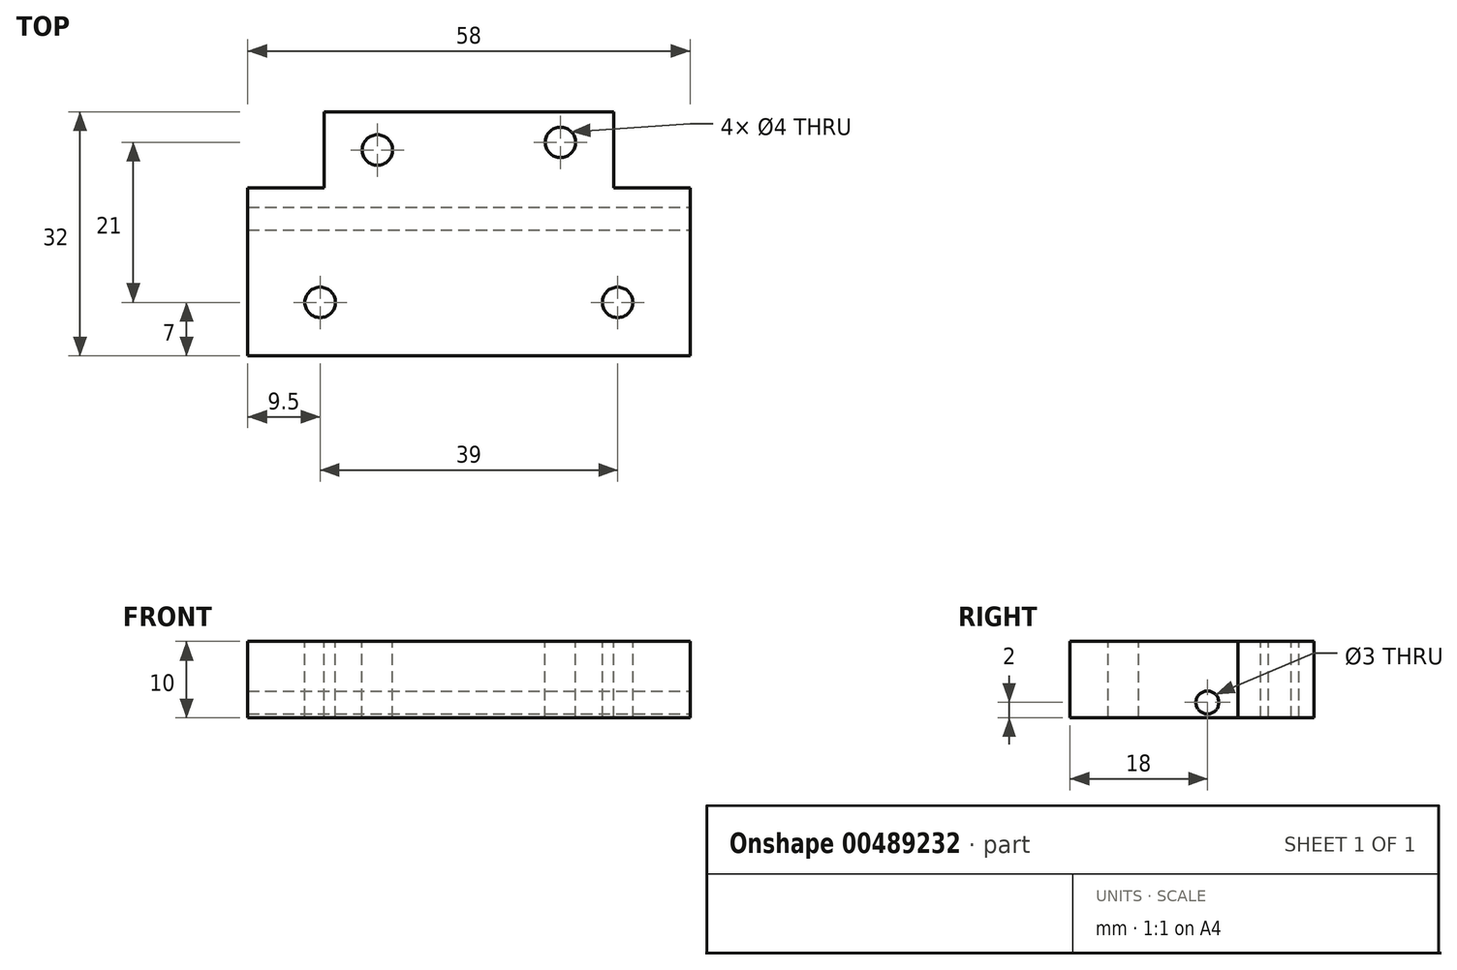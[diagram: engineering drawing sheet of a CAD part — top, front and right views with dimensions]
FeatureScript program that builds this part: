
annotation { "Feature Type Name" : "Feature", "Feature Type Description" : "" }
export const myFeature = defineFeature(function(context is Context, id is Id, definition is map)
    precondition{}
    {
        {
            var Q0;
            Q0=qCreatedBy(makeId("Top.planeOp"),FACE);
            var sketch = newSketch(context, id + "F0", { "sketchPlane" : qUnion([Q0])});
            skLineSegment(sketch, "E0.bottom", {"start": v(29, 11) * mm, "end": v(-29, 11) * mm});
            skLineSegment(sketch, "E0.top", {"start": v(29, -11) * mm, "end": v(-29, -11) * mm});
            skLineSegment(sketch, "E0.left", {"start": v(29, 11) * mm, "end": v(29, -11) * mm});
            skLineSegment(sketch, "E0.right", {"start": v(-29, 11) * mm, "end": v(-29, -11) * mm});
            skPoint(sketch, "E0.middle", {"position": v(0, 0) * mm});
            skSolve(sketch);
        }
        {
            var Q0;
            Q0 = qSketchRegion(id + "F0", true);
            extrude(context, id + "F1", {"entities" : qUnion([Q0]), "depth" : 10 * mm});
        }
        {
            var Q0;
            Q0=makeQuery(id+"F1.opExtrude","CAP_FACE",FACE,{"disambiguationData":[OSD([sQuery(id+"F0.wireOp",EDGE,"E0.bottom"),sQuery(id+"F0.wireOp",EDGE,"E0.top"),sQuery(id+"F0.wireOp",EDGE,"E0.left"),sQuery(id+"F0.wireOp",EDGE,"E0.right")])],"isStart":false});
            var sketch = newSketch(context, id + "F2", { "sketchPlane" : qUnion([Q0])});
            skCircle(sketch, "E1", {"center": v(-19.5, -4) * mm, "radius": 2 * mm});
            skCircle(sketch, "E2", {"center": v(19.5, -4) * mm, "radius": 2 * mm});
            skSolve(sketch);
        }
        {
            var Q0;
            Q0 = qSketchRegion(id + "F2", true);
            extrude(context, id + "F3", {"entities" : qUnion([Q0]), "operationType" : NewBodyOperationType.REMOVE, "oppositeDirection" : true, "depth" : 25 * mm});
        }
        {
            var Q0;
            Q0=makeQuery(id+"F1.opExtrude","SWEPT_FACE",FACE,{"disambiguationData":[OSD([sQuery(id+"F0.wireOp",EDGE,"E0.left")])]});
            var sketch = newSketch(context, id + "F4", { "sketchPlane" : qUnion([Q0])});
            skCircle(sketch, "E3", {"center": v(7, 2) * mm, "radius": 1.5 * mm});
            skSolve(sketch);
        }
        {
            var Q0;
            Q0 = qSketchRegion(id + "F4", true);
            extrude(context, id + "F5", {"entities" : qUnion([Q0]), "operationType" : NewBodyOperationType.REMOVE, "oppositeDirection" : true, "depth" : 500 * mm});
        }
        {
            var Q0;
            Q0=makeQuery(id+"F1.opExtrude","SWEPT_FACE",FACE,{"disambiguationData":[OSD([sQuery(id+"F0.wireOp",EDGE,"E0.bottom")])]});
            var sketch = newSketch(context, id + "F6", { "sketchPlane" : qUnion([Q0])});
            skLineSegment(sketch, "E4.bottom", {"start": v(-19, 0) * mm, "end": v(19, 0) * mm});
            skLineSegment(sketch, "E4.top", {"start": v(-19, 10) * mm, "end": v(19, 10) * mm});
            skLineSegment(sketch, "E4.left", {"start": v(-19, 0) * mm, "end": v(-19, 10) * mm});
            skLineSegment(sketch, "E4.right", {"start": v(19, 0) * mm, "end": v(19, 10) * mm});
            skSolve(sketch);
        }
        {
            var Q0;
            Q0 = qSketchRegion(id + "F6", true);
            extrude(context, id + "F7", {"entities" : qUnion([Q0]), "operationType" : NewBodyOperationType.ADD, "depth" : 10 * mm});
        }
        {
            var Q0;
            Q0=makeQuery(id+"F7.boolean.opBoolean","MERGE",FACE,{"derivedFrom":[makeQuery(id+"F1.opExtrude","CAP_FACE",FACE,{"disambiguationData":[OSD([sQuery(id+"F0.wireOp",EDGE,"E0.bottom"),sQuery(id+"F0.wireOp",EDGE,"E0.top"),sQuery(id+"F0.wireOp",EDGE,"E0.left"),sQuery(id+"F0.wireOp",EDGE,"E0.right")])],"isStart":false}),makeQuery(id+"F7.opExtrude","SWEPT_FACE",FACE,{"disambiguationData":[OSD([sQuery(id+"F6.wireOp",EDGE,"E4.top")])]})]});
            var sketch = newSketch(context, id + "F8", { "sketchPlane" : qUnion([Q0])});
            skCircle(sketch, "E5", {"center": v(12, 17) * mm, "radius": 2 * mm});
            skCircle(sketch, "E6", {"center": v(-12, 16) * mm, "radius": 2 * mm});
            skSolve(sketch);
        }
        {
            var Q0;
            Q0 = qSketchRegion(id + "F8", true);
            extrude(context, id + "F9", {"entities" : qUnion([Q0]), "operationType" : NewBodyOperationType.REMOVE, "oppositeDirection" : true, "depth" : 25 * mm});
        }
    });
